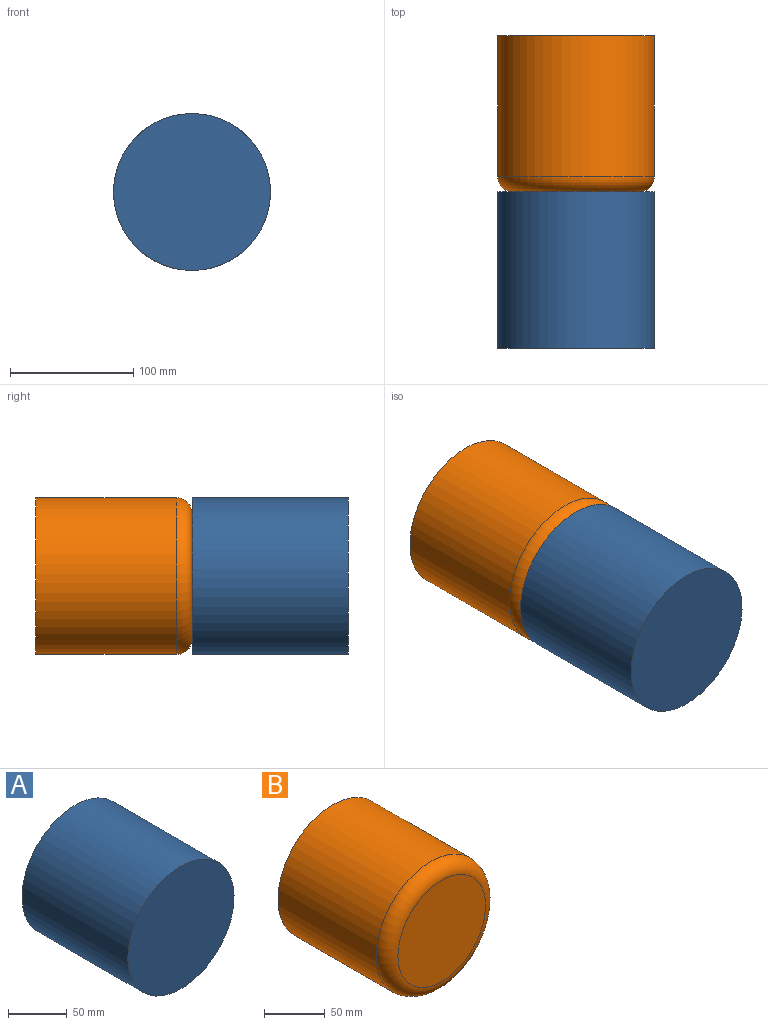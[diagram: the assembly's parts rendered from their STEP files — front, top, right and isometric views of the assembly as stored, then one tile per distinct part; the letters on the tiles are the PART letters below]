
ASSEMBLY  parts=2 mates=1
PART A: 3 faces, bbox 127.4x127x127.4 mm
  f0: cylinder r=63.72mm len=127.44mm, axis (0,1,0), area 50847.8mm2, adj f1,f2
  f1: plane 127.44x127.44mm, normal (0,-1,0), area 12756.4mm2, adj f0
  f2: plane 127.44x127.44mm, normal (0,1,0), area 12756.4mm2, adj f0
PART B: 4 faces, bbox 137.9x127x137.9 mm
  f0: cylinder r=63.72mm len=127.44mm, axis (0,1,0), area 45763mm2, adj f2,f3
  f1: plane 102.04x102.04mm, normal (0,-1,0), area 8178.3mm2, adj f3
  f2: plane 127.44x127.44mm, normal (0,1,0), area 12756.4mm2, adj f0
  f3: torus R=51.02mm, axis (0,-1,0), area 7408.7mm2, adj f0,f1
PLACE A rot(axis=(1,0,0),180deg) t=(-106.41,-249.96,2.96)mm
PLACE B t=(-106.41,4.04,2.96)mm fixed
MATE parallel B.f0 <-> A.f0  axis (0,-1,0) through (-106.41,-122.96,2.96)mm
